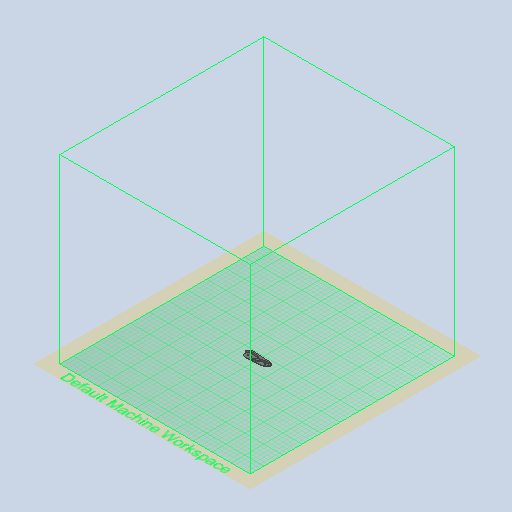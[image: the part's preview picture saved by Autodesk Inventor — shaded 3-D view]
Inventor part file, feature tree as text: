
AUTODESK INVENTOR PART (.ipt)
format: ipt  version: 2022 (Build 260153000, 153)  size: 463,872 bytes
history: native  units: in
note: dims shown in document units (in); Inventor stores cm internally (conversion verified against a paired STEP export)
features: extrude x7, sketch x7, other x1
ambient origin geometry x8: Origin, YZ Plane, XZ Plane, XY Plane, X Axis, Y Axis, Z Axis, Center Point
bodies: Body1 (feature_tree)
feature tree (15):
  other  "Sólido1"
  extrude  "Extrusión1"  Depth=0.0984in
  extrude  "Extrusión2"  Depth=0.5906in
  extrude  "Extrusión3"  Depth=0.0984in
  extrude  "Extrusión6"  Depth=0.1181in
  extrude  "Extrusión7"  Depth=0.0984in
  extrude  "Extrusión10"  Depth=0.0787in
  extrude  "Extrusión11"  Depth=0.0197in
  sketch  "Boceto1"  dims[d9=0.0984in d10=0.0984in]
  sketch  "Boceto2"  dims[d11=1.5354in d12=0.5906in]
  sketch  "Boceto3"  dims[d13=0.2362in d14=0.0984in]
  sketch  "Boceto7"  dims[d15=0.1378in d16=0.1181in]
  sketch  "Boceto8"  dims[d17=0.1575in d18=0.0984in]
  sketch  "Boceto11"  dims[d19=0.128in d20=0.0787in]
  sketch  "Boceto12"  dims[d21=0.0787in d22=0.2205in d23=0.2244in d25=0.0394in d26=0.0in d27=0.0787in d28=0.0in d31=0.2165in d32=0.0in d35=0.0984in d36=0.0787in d39=0.0984in d40=0.0984in d41=0.0591in d42=0.0in d43=0.0315in d44=0.0in d55=0.0787in d56=0.0787in d57=0.0in d59=0.0394in d60=0.0in d33=0.0197in d34=0.0344in d61=0.0197in d62=0.0344in]
